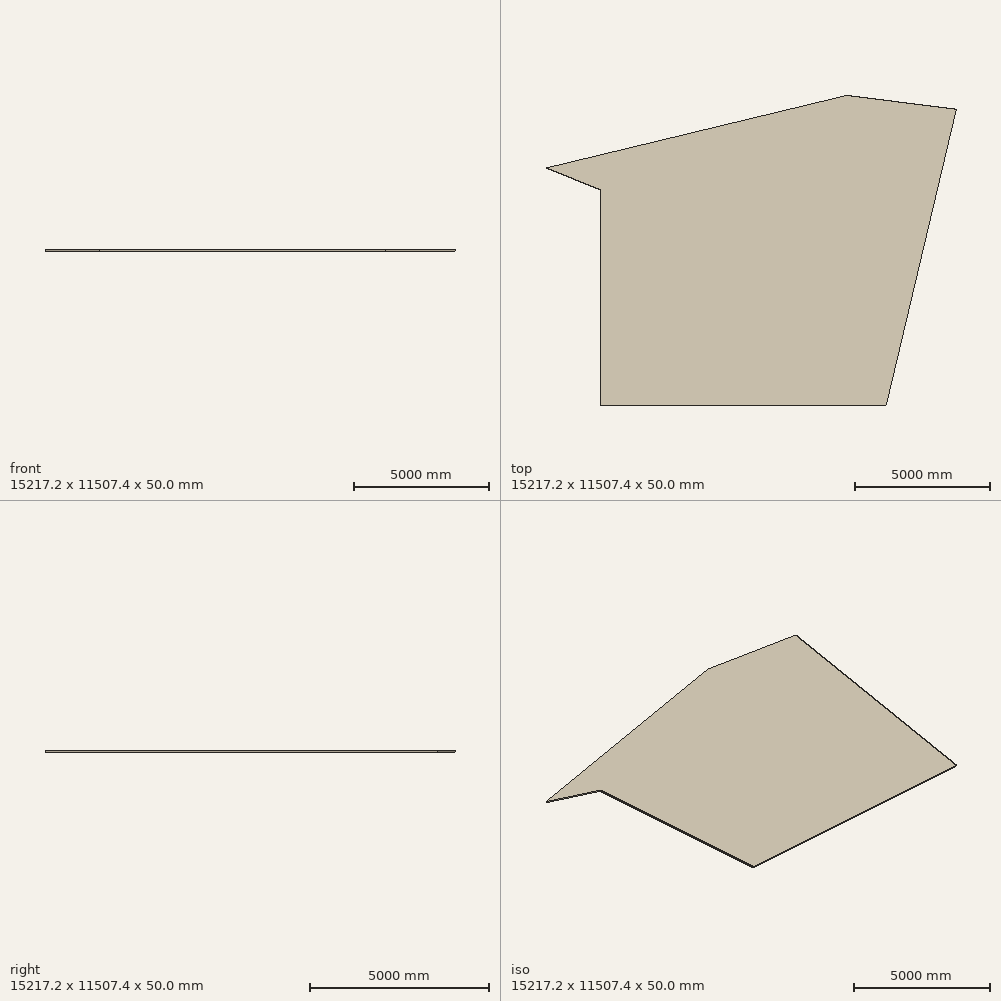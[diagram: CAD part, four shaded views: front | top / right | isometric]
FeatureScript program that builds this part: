
annotation { "Feature Type Name" : "Feature", "Feature Type Description" : "" }
export const myFeature = defineFeature(function(context is Context, id is Id, definition is map)
    precondition{}
    {
        {
            var Q0;
            Q0=qCreatedBy(makeId("Top.planeOp"),FACE);
            var sketch = newSketch(context, id + "F0", { "sketchPlane" : qUnion([Q0])});
            skLineSegment(sketch, "E0", {"start": v(-10600, 9300) * mm, "end": v(-10600, 0) * mm, "construction": true});
            skLineSegment(sketch, "E1", {"start": v(-10600, 0) * mm, "end": v(0, 0) * mm});
            skLineSegment(sketch, "E2", {"start": v(0, 0) * mm, "end": v(2605.08, 10995.62) * mm});
            skLineSegment(sketch, "E3", {"start": v(2605.08, 10995.62) * mm, "end": v(-1462.85, 11507.4) * mm});
            skLineSegment(sketch, "E4", {"start": v(-1462.85, 11507.4) * mm, "end": v(-12612.12, 8813.9) * mm});
            skLineSegment(sketch, "E5", {"start": v(-12612.12, 8813.9) * mm, "end": v(-10600, 8000) * mm});
            skLineSegment(sketch, "E6", {"start": v(-10600, 8000) * mm, "end": v(-10600, 0) * mm});
            skSolve(sketch);
        }
        {
            var Q0;
            Q0 = qSketchRegion(id + "F0", true);
            extrude(context, id + "F1", {"entities" : qUnion([Q0]), "depth" : 50 * mm});
        }
    });
